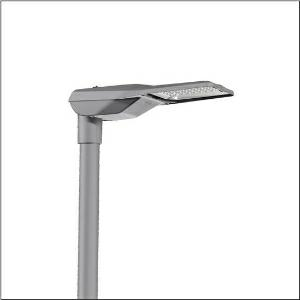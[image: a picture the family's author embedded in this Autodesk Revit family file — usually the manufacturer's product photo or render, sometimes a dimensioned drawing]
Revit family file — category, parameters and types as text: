
# Revit family: streetlight_sl_21_mini___st0_8a_5xe2c43s08hb_a304
name_source: partatom
category: Lighting Fixtures
units: mm (PartAtom-declared; Revit-internal decimal feet)

## family parameters
Cut with Voids When Loaded = No
Host = Face
Light Source = No
Part Type = Normal
Room Calculation Point = No
Round Connector Dimension = Use Diameter
Shared = No

## types (1)
- --- (1 x LED, 9430 lm, 66 W, 4000K)
    Apparent Load = 66 VA
    CIE Flux Codes = 38 75 97 100 100
    Color Rendering = 70
    Color Temperature = 4000K
    Default Elevation = 1800 mm
    Description = Streetlight SL 21 mini, mast luminaire, primary light control with lens, of PMMA, primary optical cover: cover, of toughened safety glass, transparent, light distribution: ST0.8a, light emission: direct distribution, primary light characteristic: asymmetric, installation type: side-entry, post-top, LED, High Power LED, rated luminous flux: 9.430lm, luminous efficacy: 143lm/W, light colour: 740, colour temperature: 4000K, control gear: D4i, control: overheat protection, constant luminous flux control, time-dependent luminous flux control, flexible luminous flux parameterisation, pre-setting: logarithmic dimming characteristic, mains connection: 220..240V, AC, 50/60Hz, start of lifetime: 66W, end of service life: 69W, reduction: 30W, luminaire housing, of diecast aluminium, powder-coated, Siteco® metallic grey (DB 702S), corrosivity category C5 mid according to DIN EN ISO 12944, please order mast flange separately, inclination adjustable: 0°, 5°, 10°, 15°, sealing non-destructively replaceable, multi-level sealing system, length: 628mm, width: 235mm, height: 110mm, mast flange for spigot size: 42mm (side-entry): 5XC10008XM4, 60/48mm (side-entry/post-top): 5XC10108XM2, 76/60mm (side-entry/post-top): 5XC10108XM1, mounting height: 4..8m, Smart Interface above, protection rating (complete): IP66, insulation class (complete): insulation class II (safety insulation), certification: CE, ENEC, ENEC+, VDE, impact resistance: IK10, permissible operating ambient temperature for outdoor applications: -40..+50°C, standard-compliant lighting for roads and squares, packaging unit: 1 piece

Light Distribution: ST0.8a
    Height = 110 mm
    Lamp = 1 x LED
    Lamp Light Flux = 9430 lm
    Lamp Power = 66 W
    Lamp count = 1
    Length = 625 mm
    Luminous efficacy = 143 lm/W
    Manufacturer = Siteco
    ModVariant = No
    Model = 5XE2C43S08HB
    Number of Poles = 1
    OnlyDefault = Yes
    Power Factor = 1
    Product Name = Streetlight SL 21 mini | ST0.8a
    Product group = mast luminaire | pylon top
    ProductGroupID = 6100
    Protection Class = Protection class II
    Protection Degree = IP 66
    RLX_Detail_Level = 1
    RLX_Emergency_Light_Flux = 0 lm
    RLX_Emergency_Type = 0
    RLX_Emergency_Type_DB = No
    RlxData = <blob elided: 26129 chars, md5=8898a14d>
    Socket = socket
    Standby Power = 0 W
    System Light Flux = 9430 lm
    System Power = 66 W
    Type Comments = factory setting: luminous flux: 100 % | dim-lin: 254 | 670 mA
    Type Image = l_1003515.jpg
    URL = http://relux.com
    VarID = @adj_185454
    Voltage = 0 V
    Weight = 0.00 kg
    Width = 234 mm

## geometry (parser evidence)
native form markers: Blend x4, Sweep x11
no freeform markers — native parametric forms only
